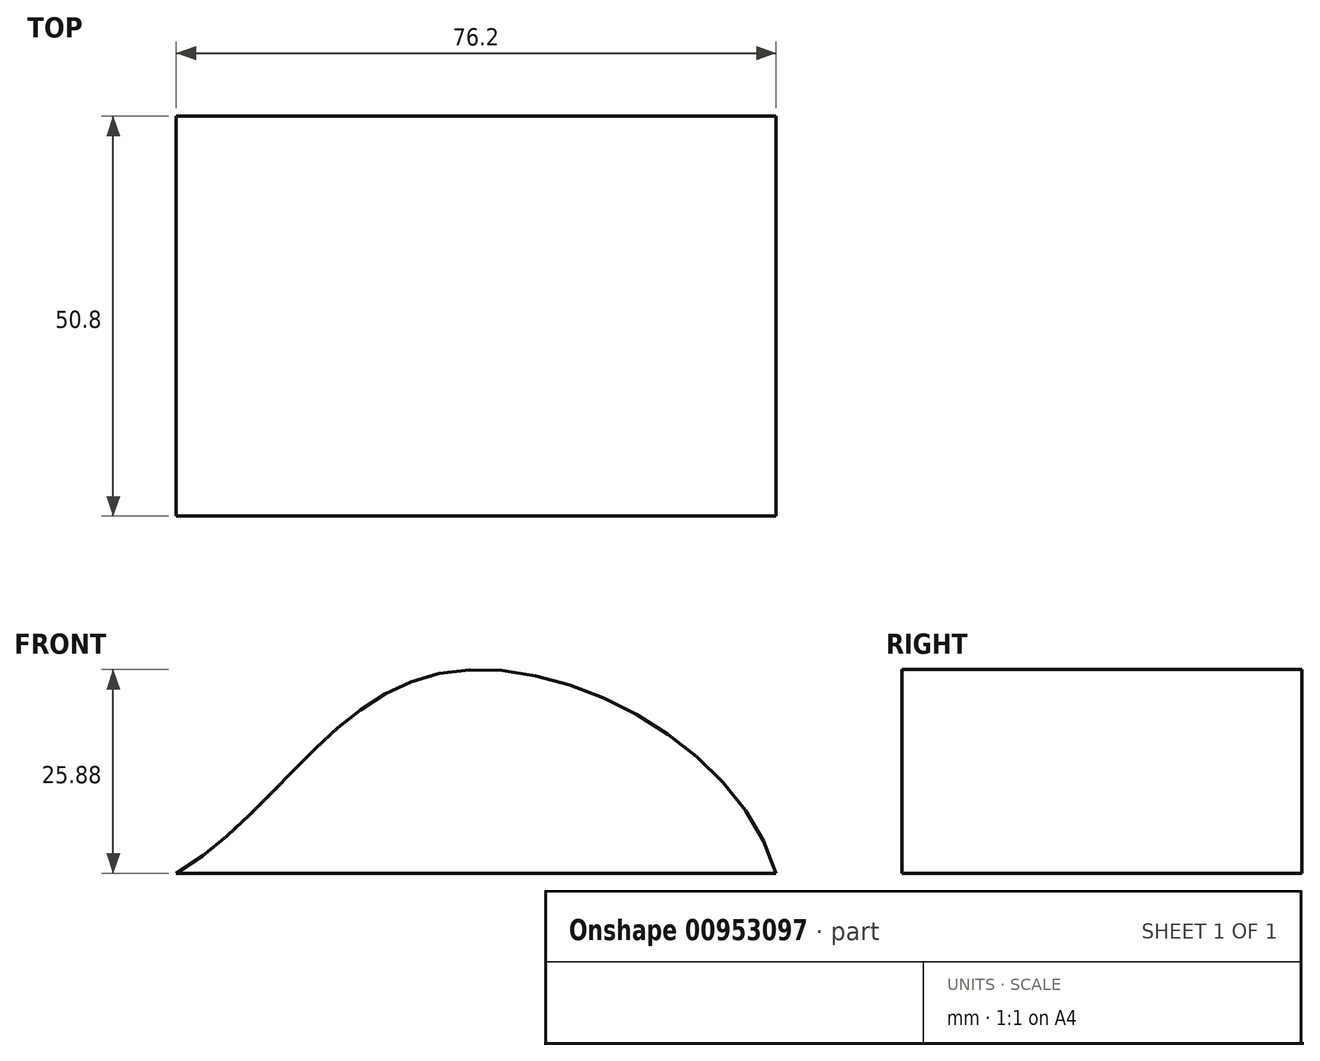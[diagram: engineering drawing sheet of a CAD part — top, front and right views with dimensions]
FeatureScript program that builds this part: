
annotation { "Feature Type Name" : "Feature", "Feature Type Description" : "" }
export const myFeature = defineFeature(function(context is Context, id is Id, definition is map)
    precondition{}
    {
        {
            var Q0;
            Q0=qCreatedBy(makeId("Front.planeOp"),FACE);
            var sketch = newSketch(context, id + "F0", { "sketchPlane" : qUnion([Q0])});
            skFitSpline(sketch, "E0", {"points": [v(0, 0) * mm, v(33.43, 25.4) * mm, v(76.2, 0) * mm], "startDerivative": vector(79.57, 47.74) * mm, "endDerivative": vector(29.24, -97.31) * mm});
            skLineSegment(sketch, "E1", {"start": v(0, 0) * mm, "end": v(76.2, 0) * mm});
            skSolve(sketch);
        }
        {
            var Q0;
            Q0 = qSketchRegion(id + "F0", true);
            extrude(context, id + "F1", {"entities" : qUnion([Q0]), "depth" : 50.8 * mm, "offsetDistance" : 25.4 * mm});
        }
    });
